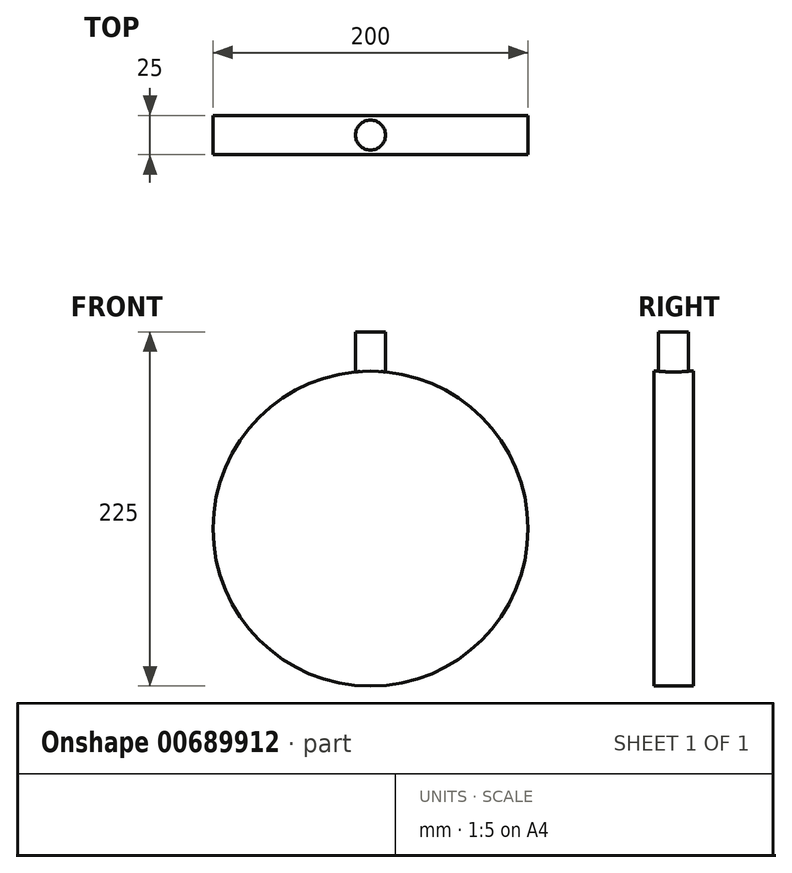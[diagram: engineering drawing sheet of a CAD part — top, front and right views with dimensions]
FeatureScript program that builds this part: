
annotation { "Feature Type Name" : "Feature", "Feature Type Description" : "" }
export const myFeature = defineFeature(function(context is Context, id is Id, definition is map)
    precondition{}
    {
        {
            var Q0;
            Q0=qCreatedBy(makeId("Front.planeOp"),FACE);
            var sketch = newSketch(context, id + "F0", { "sketchPlane" : qUnion([Q0])});
            skCircle(sketch, "E0", {"center": v(0, 0) * mm, "radius": 100 * mm});
            skSolve(sketch);
        }
        {
            var Q0;
            Q0=makeQuery(id+"F0.imprint","IMPRINT",FACE,{"disambiguationData":[TD([[makeQuery(id+"F0.imprint","IMPRINT",EDGE,{"derivedFrom":sQuery(id+"F0.wireOp",EDGE,"E0")}),1.0]])]});
            extrude(context, id + "F1", {"entities" : qUnion([Q0]), "depth" : 12.5 * mm, "offsetDistance" : 25 * mm});
        }
        {
            var Q0;
            Q0=makeQuery(id+"F1.opExtrude","CAP_FACE",FACE,{"disambiguationData":[OSD([sQuery(id+"F0.wireOp",EDGE,"E0")])],"isStart":true});
            extrude(context, id + "F2", {"entities" : qUnion([Q0]), "operationType" : NewBodyOperationType.ADD, "depth" : 12.5 * mm, "offsetDistance" : 25 * mm});
        }
        {
            var Q0;
            Q0=qCreatedBy(makeId("Top.planeOp"),FACE);
            var sketch = newSketch(context, id + "F3", { "sketchPlane" : qUnion([Q0])});
            skCircle(sketch, "E1", {"center": v(0, 0) * mm, "radius": 9.5 * mm});
            skSolve(sketch);
        }
        {
            var Q0;
            Q0 = qSketchRegion(id + "F3", true);
            extrude(context, id + "F4", {"entities" : qUnion([Q0]), "operationType" : NewBodyOperationType.ADD, "depth" : 125 * mm, "offsetDistance" : 25 * mm});
        }
    });
